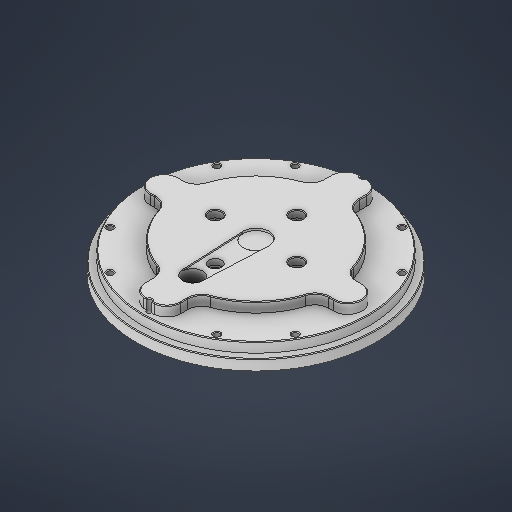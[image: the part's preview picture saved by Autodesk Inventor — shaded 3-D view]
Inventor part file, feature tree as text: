
AUTODESK INVENTOR PART (.ipt)
format: ipt  version: 2025 (Build 290162000, 162)  size: 523,776 bytes
history: native  units: in
note: dims shown in document units (in); Inventor stores cm internally (conversion verified against a paired STEP export)
features: sketch x14, extrude x9, hole x4, chamfer x3
ambient origin geometry x8: Origin, YZ Plane, XZ Plane, XY Plane, X Axis, Y Axis, Z Axis, Center Point
bodies: Solid1 (feature_tree)
feature tree (30):
  sketch  "Sketch1"  dims[d3=4.3307in d24=6.6929in]
  extrude  "Extrusion1"  Depth=6.6929in
  extrude  "Extrusion2"  Depth=5.9843in
  extrude  "Extrusion3"  Depth=4.3307in
  sketch  "Sketch2"  dims[d27=0.9843in d28=4.3307in]
  extrude  "Extrusion4"  Depth=0.3937in
  hole  "Hole1"  [1 undecoded]
  hole  "Hole2"  [1 undecoded]
  sketch  "Sketch4"  dims[d38=0.2953in d39=0.0in d40=2.2835in]
  extrude  "Extrusion5"  Depth=2.2835in
  extrude  "Extrusion6"  Depth=0.1969in
  hole  "Hole3"  [1 undecoded]
  chamfer  "Chamfer1"  Distance=0.7874in Angle=360.0deg
  chamfer  "Chamfer2"  Distance=0.1969in
  hole  "Hole5"  [1 undecoded]
  extrude  "Extrusion9"  Depth=0.0591in TaperAngle=0.0deg
  extrude  "Extrusion10"  Depth=0.0197in TaperAngle=0.0deg
  chamfer  "Chamfer4"  Distance=0.1969in
  extrude  "Extrusion11"  Depth=0.0197in TaperAngle=360.0deg
  sketch  "Sketch Circular Pattern1"  dims[d25=6.2992in d26=5.9843in]
  sketch  "Sketch3"  dims[d31=0.3937in d32=0.3937in]
  sketch  "Sketch Circular Pattern2"  dims[d29=0.7874in d30=0.3937in]
  sketch  "Sketch5"  dims[d41=0.3543in d42=0.1969in]
  sketch  "Sketch Circular Pattern3"  dims[d34=0.8465in d35=0.0in d36=0.5709in d37=0.0in]
  sketch  "Sketch7"  dims[d56=5.9843in]
  sketch  "Sketch Circular Pattern5"  dims[d43=1.5748in d45=360.0deg d47=0.1969in d48=0.0in]
  sketch  "Sketch9"  dims[d57=0.1378in d58=0.7874in d60=360.0deg]
  sketch  "Sketch Circular Pattern6"  dims[d49=0.2165in d50=0.7874in d51=0.1575in d52=0.0787in d53=90.0deg d54=0.315in d55=0.8108in]
  sketch  "Sketch10"  dims[d62=0.1276in d63=0.315in d64=0.1575in d65=0.0787in d66=90.0deg d67=0.4646in d68=0.8108in]
  sketch  "Sketch11"  dims[d69=3.2283in d70=0.1969in d71=0.7874in d72=0.0591in d73=0.0in d74=0.4724in d75=0.0in d76=0.1969in d77=4.7244in d79=360.0deg d81=0.1628in d82=0.3937in d83=0.1575in d84=0.0787in d85=90.0deg d86=0.3937in d87=0.8108in d88=0.0197in d89=0.0787in d90=45.0deg d91=0.0197in d92=0.0787in d93=45.0deg d107=3.7402in d108=0.1969in d109=6.2992in d111=360.0deg d113=0.1969in d114=0.7874in d115=0.748in d116=0.3543in d117=90.0deg d118=0.7874in d119=0.8108in d139=0.7185in d140=3.1496in d141=0.7185in d142=3.1496in d144=360.0deg d146=0.0591in d147=0.0in d151=0.5512in d152=1.7717in d153=0.0in d154=0.0in d155=0.0197in d156=0.0787in d157=45.0deg d158=0.5512in d159=1.7717in d160=0.0394in d161=0.0in d162=0.1969in d137=0.0197in d138=0.0344in]
note: 4 required parameter values undecoded (feature->parameter linkage not recoverable at this tier; creation-order binding heuristic only, values carry confidence <= 0.55)
